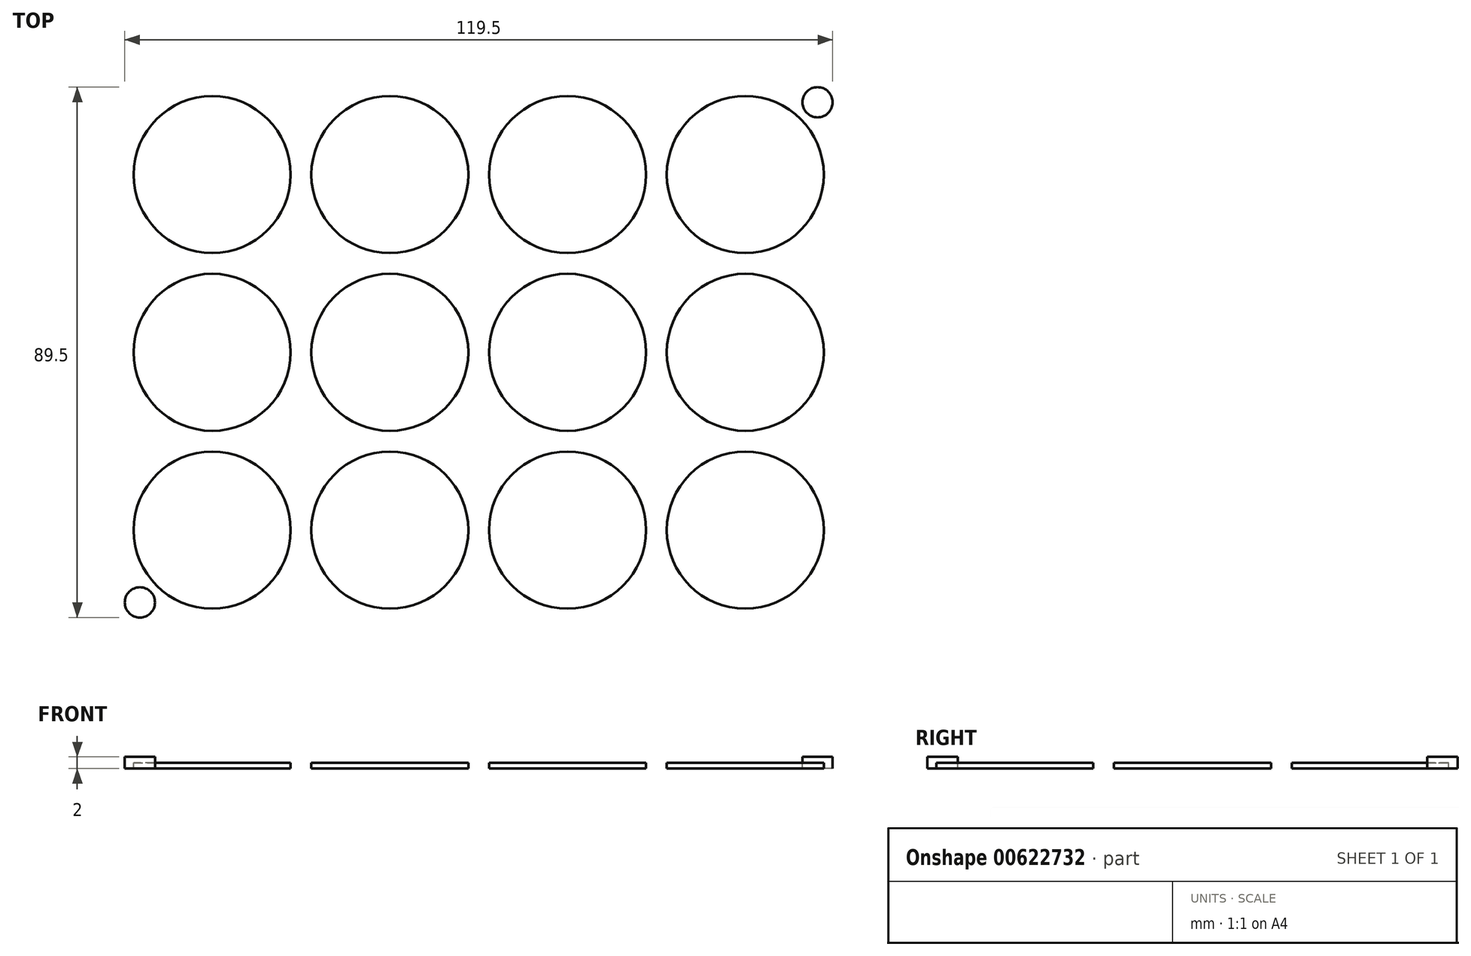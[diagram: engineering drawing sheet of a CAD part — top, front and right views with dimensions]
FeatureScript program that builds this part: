
annotation { "Feature Type Name" : "Feature", "Feature Type Description" : "" }
export const myFeature = defineFeature(function(context is Context, id is Id, definition is map)
    precondition{}
    {
        {
            var Q0;
            Q0=qCreatedBy(makeId("Top.planeOp"),FACE);
            var sketch = newSketch(context, id + "F0", { "sketchPlane" : qUnion([Q0])});
            skLineSegment(sketch, "E0.bottom", {"start": v(-61.25, 46.25) * mm, "end": v(61.25, 46.25) * mm});
            skLineSegment(sketch, "E0.top", {"start": v(-61.25, -46.25) * mm, "end": v(61.25, -46.25) * mm});
            skLineSegment(sketch, "E0.left", {"start": v(-61.25, 46.25) * mm, "end": v(-61.25, -46.25) * mm});
            skLineSegment(sketch, "E0.right", {"start": v(61.25, 46.25) * mm, "end": v(61.25, -46.25) * mm});
            skPoint(sketch, "E0.middle", {"position": v(0, 0) * mm});
            skCircle(sketch, "E1", {"center": v(-45, 30) * mm, "radius": 13.25 * mm});
            skCircle(sketch, "E2.0.1.0", {"center": v(-45, 0) * mm, "radius": 13.25 * mm});
            skCircle(sketch, "E2.0.2.0", {"center": v(-45, -30) * mm, "radius": 13.25 * mm});
            skCircle(sketch, "E2.1.0.0", {"center": v(-15, 30) * mm, "radius": 13.25 * mm});
            skCircle(sketch, "E2.1.1.0", {"center": v(-15, 0) * mm, "radius": 13.25 * mm});
            skCircle(sketch, "E2.1.2.0", {"center": v(-15, -30) * mm, "radius": 13.25 * mm});
            skCircle(sketch, "E2.2.0.0", {"center": v(15, 30) * mm, "radius": 13.25 * mm});
            skCircle(sketch, "E2.2.1.0", {"center": v(15, 0) * mm, "radius": 13.25 * mm});
            skCircle(sketch, "E2.2.2.0", {"center": v(15, -30) * mm, "radius": 13.25 * mm});
            skCircle(sketch, "E2.3.0.0", {"center": v(45, 30) * mm, "radius": 13.25 * mm});
            skCircle(sketch, "E2.3.1.0", {"center": v(45, 0) * mm, "radius": 13.25 * mm});
            skCircle(sketch, "E2.3.2.0", {"center": v(45, -30) * mm, "radius": 13.25 * mm});
            skLineSegment(sketch, "E2.direction1", {"start": v(-45, 30) * mm, "end": v(-15, 30) * mm, "construction": true});
            skLineSegment(sketch, "E2.direction2", {"start": v(-45, 30) * mm, "end": v(-45, 0) * mm, "construction": true});
            skSolve(sketch);
        }
        {
            var Q0;
            Q0=makeQuery(id+"F0.imprint","IMPRINT",FACE,{"disambiguationData":[TD([[makeQuery(id+"F0.imprint","IMPRINT",EDGE,{"derivedFrom":sQuery(id+"F0.wireOp",EDGE,"E1")}),1.0]])]});
            var Q1;
            Q1=makeQuery(id+"F0.imprint","IMPRINT",FACE,{"disambiguationData":[TD([[makeQuery(id+"F0.imprint","IMPRINT",EDGE,{"derivedFrom":sQuery(id+"F0.wireOp",EDGE,"E2.1.0.0")}),1.0]])]});
            var Q2;
            Q2=makeQuery(id+"F0.imprint","IMPRINT",FACE,{"disambiguationData":[TD([[makeQuery(id+"F0.imprint","IMPRINT",EDGE,{"derivedFrom":sQuery(id+"F0.wireOp",EDGE,"E2.2.0.0")}),1.0]])]});
            var Q3;
            Q3=makeQuery(id+"F0.imprint","IMPRINT",FACE,{"disambiguationData":[TD([[makeQuery(id+"F0.imprint","IMPRINT",EDGE,{"derivedFrom":sQuery(id+"F0.wireOp",EDGE,"E2.3.0.0")}),1.0]])]});
            var Q4;
            Q4=makeQuery(id+"F0.imprint","IMPRINT",FACE,{"disambiguationData":[TD([[makeQuery(id+"F0.imprint","IMPRINT",EDGE,{"derivedFrom":sQuery(id+"F0.wireOp",EDGE,"E2.4.0.0")}),1.0]])]});
            var Q5;
            Q5=makeQuery(id+"F0.imprint","IMPRINT",FACE,{"disambiguationData":[TD([[makeQuery(id+"F0.imprint","IMPRINT",EDGE,{"derivedFrom":sQuery(id+"F0.wireOp",EDGE,"E2.4.1.0")}),1.0]])]});
            var Q6;
            Q6=makeQuery(id+"F0.imprint","IMPRINT",FACE,{"disambiguationData":[TD([[makeQuery(id+"F0.imprint","IMPRINT",EDGE,{"derivedFrom":sQuery(id+"F0.wireOp",EDGE,"E2.3.1.0")}),1.0]])]});
            var Q7;
            Q7=makeQuery(id+"F0.imprint","IMPRINT",FACE,{"disambiguationData":[TD([[makeQuery(id+"F0.imprint","IMPRINT",EDGE,{"derivedFrom":sQuery(id+"F0.wireOp",EDGE,"E0.bottom")}),-1.0]])]});
            var Q8;
            Q8=makeQuery(id+"F0.imprint","IMPRINT",FACE,{"disambiguationData":[TD([[makeQuery(id+"F0.imprint","IMPRINT",EDGE,{"derivedFrom":sQuery(id+"F0.wireOp",EDGE,"E2.1.1.0")}),1.0]])]});
            var Q9;
            Q9=makeQuery(id+"F0.imprint","IMPRINT",FACE,{"disambiguationData":[TD([[makeQuery(id+"F0.imprint","IMPRINT",EDGE,{"derivedFrom":sQuery(id+"F0.wireOp",EDGE,"E2.0.1.0")}),1.0]])]});
            var Q10;
            Q10=makeQuery(id+"F0.imprint","IMPRINT",FACE,{"disambiguationData":[TD([[makeQuery(id+"F0.imprint","IMPRINT",EDGE,{"derivedFrom":sQuery(id+"F0.wireOp",EDGE,"E2.2.1.0")}),1.0]])]});
            var Q11;
            Q11=makeQuery(id+"F0.imprint","IMPRINT",FACE,{"disambiguationData":[TD([[makeQuery(id+"F0.imprint","IMPRINT",EDGE,{"derivedFrom":sQuery(id+"F0.wireOp",EDGE,"E2.2.2.0")}),1.0]])]});
            var Q12;
            Q12=makeQuery(id+"F0.imprint","IMPRINT",FACE,{"disambiguationData":[TD([[makeQuery(id+"F0.imprint","IMPRINT",EDGE,{"derivedFrom":sQuery(id+"F0.wireOp",EDGE,"E2.1.2.0")}),1.0]])]});
            var Q13;
            Q13=makeQuery(id+"F0.imprint","IMPRINT",FACE,{"disambiguationData":[TD([[makeQuery(id+"F0.imprint","IMPRINT",EDGE,{"derivedFrom":sQuery(id+"F0.wireOp",EDGE,"E2.0.2.0")}),1.0]])]});
            var Q14;
            Q14=makeQuery(id+"F0.imprint","IMPRINT",FACE,{"disambiguationData":[TD([[makeQuery(id+"F0.imprint","IMPRINT",EDGE,{"derivedFrom":sQuery(id+"F0.wireOp",EDGE,"E2.3.2.0")}),1.0]])]});
            var Q15;
            Q15=makeQuery(id+"F0.imprint","IMPRINT",FACE,{"disambiguationData":[TD([[makeQuery(id+"F0.imprint","IMPRINT",EDGE,{"derivedFrom":sQuery(id+"F0.wireOp",EDGE,"E2.4.2.0")}),1.0]])]});
            var Q16;
            Q16=makeQuery(id+"F0.imprint","IMPRINT",FACE,{"disambiguationData":[TD([[makeQuery(id+"F0.imprint","IMPRINT",EDGE,{"derivedFrom":sQuery(id+"F0.wireOp",EDGE,"E2.3.3.0")}),1.0]])]});
            var Q17;
            Q17=makeQuery(id+"F0.imprint","IMPRINT",FACE,{"disambiguationData":[TD([[makeQuery(id+"F0.imprint","IMPRINT",EDGE,{"derivedFrom":sQuery(id+"F0.wireOp",EDGE,"E2.4.3.0")}),1.0]])]});
            var Q18;
            Q18=makeQuery(id+"F0.imprint","IMPRINT",FACE,{"disambiguationData":[TD([[makeQuery(id+"F0.imprint","IMPRINT",EDGE,{"derivedFrom":sQuery(id+"F0.wireOp",EDGE,"E2.4.4.0")}),1.0]])]});
            var Q19;
            Q19=makeQuery(id+"F0.imprint","IMPRINT",FACE,{"disambiguationData":[TD([[makeQuery(id+"F0.imprint","IMPRINT",EDGE,{"derivedFrom":sQuery(id+"F0.wireOp",EDGE,"E2.3.4.0")}),1.0]])]});
            var Q20;
            Q20=makeQuery(id+"F0.imprint","IMPRINT",FACE,{"disambiguationData":[TD([[makeQuery(id+"F0.imprint","IMPRINT",EDGE,{"derivedFrom":sQuery(id+"F0.wireOp",EDGE,"E2.2.4.0")}),1.0]])]});
            var Q21;
            Q21=makeQuery(id+"F0.imprint","IMPRINT",FACE,{"disambiguationData":[TD([[makeQuery(id+"F0.imprint","IMPRINT",EDGE,{"derivedFrom":sQuery(id+"F0.wireOp",EDGE,"E2.2.3.0")}),1.0]])]});
            var Q22;
            Q22=makeQuery(id+"F0.imprint","IMPRINT",FACE,{"disambiguationData":[TD([[makeQuery(id+"F0.imprint","IMPRINT",EDGE,{"derivedFrom":sQuery(id+"F0.wireOp",EDGE,"E2.1.4.0")}),1.0]])]});
            var Q23;
            Q23=makeQuery(id+"F0.imprint","IMPRINT",FACE,{"disambiguationData":[TD([[makeQuery(id+"F0.imprint","IMPRINT",EDGE,{"derivedFrom":sQuery(id+"F0.wireOp",EDGE,"E2.1.3.0")}),1.0]])]});
            var Q24;
            Q24=makeQuery(id+"F0.imprint","IMPRINT",FACE,{"disambiguationData":[TD([[makeQuery(id+"F0.imprint","IMPRINT",EDGE,{"derivedFrom":sQuery(id+"F0.wireOp",EDGE,"E2.0.3.0")}),1.0]])]});
            var Q25;
            Q25=makeQuery(id+"F0.imprint","IMPRINT",FACE,{"disambiguationData":[TD([[makeQuery(id+"F0.imprint","IMPRINT",EDGE,{"derivedFrom":sQuery(id+"F0.wireOp",EDGE,"E2.0.4.0")}),1.0]])]});
            extrude(context, id + "F1", {"entities" : qUnion([Q0, Q1, Q2, Q3, Q4, Q5, Q6, Q7, Q8, Q9, Q10, Q11, Q12, Q13, Q14, Q15, Q16, Q17, Q18, Q19, Q20, Q21, Q22, Q23, Q24, Q25]), "depth" : 1 * mm, "offsetDistance" : 25 * mm});
        }
        {
            var Q0;
            Q0=qSketchRegion(id+"F0",true);
            extrude(context, id + "F2", {"entities" : qUnion([Q0]), "operationType" : NewBodyOperationType.ADD, "depth" : 2 * mm, "offsetDistance" : 25 * mm});
        }
        {
            var Q0;
            Q0=makeQuery(id+"F2.opExtrude","CAP_FACE",FACE,{"disambiguationData":[OSD([sQuery(id+"F0.wireOp",EDGE,"E0.bottom"),sQuery(id+"F0.wireOp",EDGE,"E0.top"),sQuery(id+"F0.wireOp",EDGE,"E0.left"),sQuery(id+"F0.wireOp",EDGE,"E0.right"),sQuery(id+"F0.wireOp",EDGE,"E1"),sQuery(id+"F0.wireOp",EDGE,"E2.0.1.0"),sQuery(id+"F0.wireOp",EDGE,"E2.0.2.0"),sQuery(id+"F0.wireOp",EDGE,"E2.0.3.0"),sQuery(id+"F0.wireOp",EDGE,"E2.0.4.0"),sQuery(id+"F0.wireOp",EDGE,"E2.1.0.0"),sQuery(id+"F0.wireOp",EDGE,"E2.1.1.0"),sQuery(id+"F0.wireOp",EDGE,"E2.1.2.0"),sQuery(id+"F0.wireOp",EDGE,"E2.1.3.0"),sQuery(id+"F0.wireOp",EDGE,"E2.1.4.0"),sQuery(id+"F0.wireOp",EDGE,"E2.2.0.0"),sQuery(id+"F0.wireOp",EDGE,"E2.2.1.0"),sQuery(id+"F0.wireOp",EDGE,"E2.2.2.0"),sQuery(id+"F0.wireOp",EDGE,"E2.2.3.0"),sQuery(id+"F0.wireOp",EDGE,"E2.2.4.0"),sQuery(id+"F0.wireOp",EDGE,"E2.3.0.0"),sQuery(id+"F0.wireOp",EDGE,"E2.3.1.0"),sQuery(id+"F0.wireOp",EDGE,"E2.3.2.0"),sQuery(id+"F0.wireOp",EDGE,"E2.3.3.0"),sQuery(id+"F0.wireOp",EDGE,"E2.3.4.0"),sQuery(id+"F0.wireOp",EDGE,"E2.4.0.0"),sQuery(id+"F0.wireOp",EDGE,"E2.4.1.0"),sQuery(id+"F0.wireOp",EDGE,"E2.4.2.0"),sQuery(id+"F0.wireOp",EDGE,"E2.4.3.0"),sQuery(id+"F0.wireOp",EDGE,"E2.4.4.0")])],"isStart":false});
            var sketch = newSketch(context, id + "F3", { "sketchPlane" : qUnion([Q0])});
            skLineSegment(sketch, "E3", {"start": v(0, 74.2) * mm, "end": v(0, -73.43) * mm, "construction": true});
            skLineSegment(sketch, "E4", {"start": v(-81.9, 0) * mm, "end": v(78.5, 0) * mm, "construction": true});
            skCircle(sketch, "E5", {"center": v(-57.2, 42.2) * mm, "radius": 2.55 * mm});
            skCircle(sketch, "E6.MirrorC", {"center": v(57.2, 42.2) * mm, "radius": 2.55 * mm});
            skCircle(sketch, "E7.MirrorC", {"center": v(57.2, -42.2) * mm, "radius": 2.55 * mm});
            skCircle(sketch, "E8.MirrorC", {"center": v(-57.2, -42.2) * mm, "radius": 2.55 * mm});
            skSolve(sketch);
        }
        {
            var Q0;
            Q0=makeQuery(id+"F3.imprint","IMPRINT",FACE,{"disambiguationData":[TD([[makeQuery(id+"F3.imprint","IMPRINT",EDGE,{"derivedFrom":sQuery(id+"F3.wireOp",EDGE,"E5")}),1.0]])]});
            var Q1;
            Q1=makeQuery(id+"F3.imprint","IMPRINT",FACE,{"disambiguationData":[TD([[makeQuery(id+"F3.imprint","IMPRINT",EDGE,{"derivedFrom":sQuery(id+"F3.wireOp",EDGE,"E6.MirrorC")}),-1.0]])]});
            var Q2;
            Q2=makeQuery(id+"F3.imprint","IMPRINT",FACE,{"disambiguationData":[TD([[makeQuery(id+"F3.imprint","IMPRINT",EDGE,{"derivedFrom":sQuery(id+"F3.wireOp",EDGE,"2e68c3d5-25cd-40bd-9945-6fc11be80f0a0.MirrorC")}),-1.0]])]});
            var Q3;
            Q3=makeQuery(id+"F3.imprint","IMPRINT",FACE,{"disambiguationData":[TD([[makeQuery(id+"F3.imprint","IMPRINT",EDGE,{"derivedFrom":sQuery(id+"F3.wireOp",EDGE,"QxaMrl3A-AtRa-trL4-GzdF-NhNgddZBNQFQ")}),1.0]])]});
            var Q4;
            Q4=makeQuery(id+"F3.imprint","IMPRINT",FACE,{"disambiguationData":[TD([[makeQuery(id+"F3.imprint","IMPRINT",EDGE,{"derivedFrom":sQuery(id+"F3.wireOp",EDGE,"839e4620-8980-43f4-94e8-6378de930a700.MirrorC")}),1.0]])]});
            var Q5;
            Q5=makeQuery(id+"F3.imprint","IMPRINT",FACE,{"disambiguationData":[TD([[makeQuery(id+"F3.imprint","IMPRINT",EDGE,{"derivedFrom":sQuery(id+"F3.wireOp",EDGE,"e168a04d-0960-4fc3-8a07-1196803d19df0.MirrorC")}),-1.0]])]});
            var Q6;
            Q6=makeQuery(id+"F3.imprint","IMPRINT",FACE,{"disambiguationData":[TD([[makeQuery(id+"F3.imprint","IMPRINT",EDGE,{"derivedFrom":sQuery(id+"F3.wireOp",EDGE,"E8.MirrorC")}),-1.0]])]});
            var Q7;
            Q7=makeQuery(id+"F3.imprint","IMPRINT",FACE,{"disambiguationData":[TD([[makeQuery(id+"F3.imprint","IMPRINT",EDGE,{"derivedFrom":sQuery(id+"F3.wireOp",EDGE,"E7.MirrorC")}),1.0]])]});
            extrude(context, id + "F4", {"entities" : qUnion([Q0, Q1, Q2, Q3, Q4, Q5, Q6, Q7]), "operationType" : NewBodyOperationType.REMOVE, "endBound" : BoundingType.THROUGH_ALL, "oppositeDirection" : true, "depth" : 25 * mm, "offsetDistance" : 25 * mm});
        }
    });
